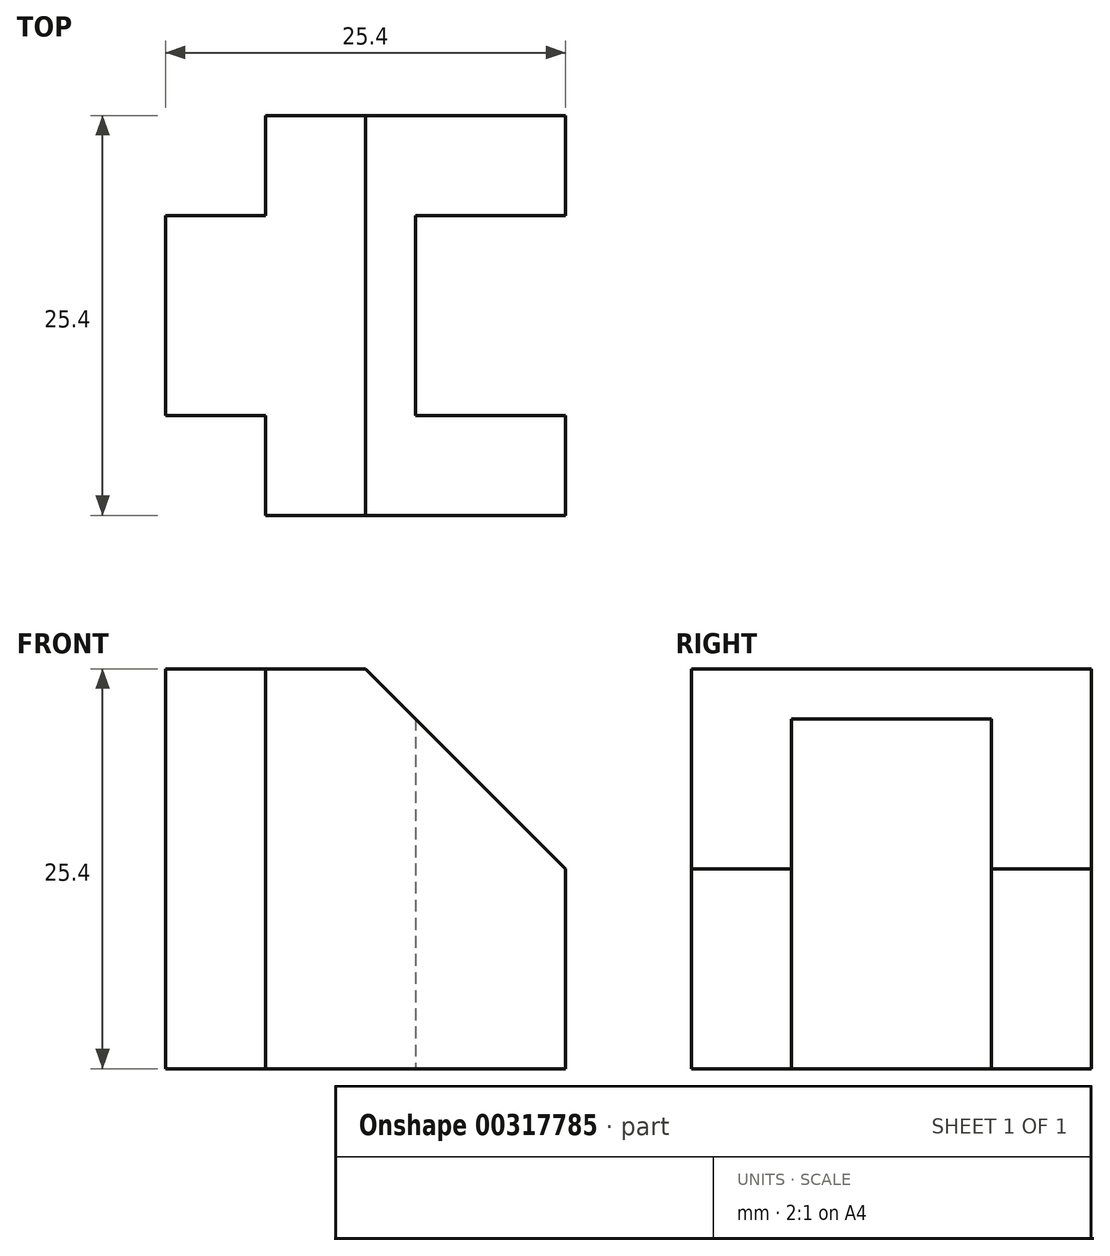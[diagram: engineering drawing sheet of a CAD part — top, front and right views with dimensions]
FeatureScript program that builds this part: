
annotation { "Feature Type Name" : "Feature", "Feature Type Description" : "" }
export const myFeature = defineFeature(function(context is Context, id is Id, definition is map)
    precondition{}
    {
        {
            var Q0;
            Q0=qCreatedBy(makeId("Front.planeOp"),FACE);
            var sketch = newSketch(context, id + "F0", { "sketchPlane" : qUnion([Q0])});
            skLineSegment(sketch, "E0", {"start": v(0, 0) * mm, "end": v(0, -25.4) * mm});
            skLineSegment(sketch, "E1", {"start": v(0, -25.4) * mm, "end": v(25.4, -25.4) * mm});
            skLineSegment(sketch, "E2", {"start": v(25.4, -25.4) * mm, "end": v(25.4, -12.7) * mm});
            skLineSegment(sketch, "E3", {"start": v(25.4, -12.7) * mm, "end": v(12.7, 0) * mm});
            skLineSegment(sketch, "E4", {"start": v(12.7, 0) * mm, "end": v(0, 0) * mm});
            skSolve(sketch);
        }
        {
            var Q0;
            Q0=makeQuery(id+"F0.imprint","IMPRINT",FACE,{"disambiguationData":[TD([[makeQuery(id+"F0.imprint","IMPRINT",EDGE,{"derivedFrom":sQuery(id+"F0.wireOp",EDGE,"E0")}),1.0]])]});
            extrude(context, id + "F1", {"entities" : qUnion([Q0]), "oppositeDirection" : true, "depth" : 25.4 * mm});
        }
        {
            var Q0;
            Q0=makeQuery(id+"F1.opExtrude","SWEPT_FACE",FACE,{"disambiguationData":[OSD([sQuery(id+"F0.wireOp",EDGE,"E4")])]});
            var sketch = newSketch(context, id + "F2", { "sketchPlane" : qUnion([Q0])});
            skLineSegment(sketch, "E5.bottom", {"start": v(0, 0) * mm, "end": v(6.35, 0) * mm});
            skLineSegment(sketch, "E5.top", {"start": v(0, 6.35) * mm, "end": v(6.35, 6.35) * mm});
            skLineSegment(sketch, "E5.left", {"start": v(0, 0) * mm, "end": v(0, 6.35) * mm});
            skLineSegment(sketch, "E5.right", {"start": v(6.35, 0) * mm, "end": v(6.35, 6.35) * mm});
            skLineSegment(sketch, "E6.bottom", {"start": v(0, 25.4) * mm, "end": v(6.35, 25.4) * mm});
            skLineSegment(sketch, "E6.top", {"start": v(0, 19.05) * mm, "end": v(6.35, 19.05) * mm});
            skLineSegment(sketch, "E6.left", {"start": v(0, 25.4) * mm, "end": v(0, 19.05) * mm});
            skLineSegment(sketch, "E6.right", {"start": v(6.35, 25.4) * mm, "end": v(6.35, 19.05) * mm});
            skSolve(sketch);
        }
        {
            var Q0;
            Q0=makeQuery(id+"F2.imprint","IMPRINT",FACE,{"disambiguationData":[TD([[makeQuery(id+"F2.imprint","IMPRINT",EDGE,{"derivedFrom":sQuery(id+"F2.wireOp",EDGE,"E6.bottom")}),1.0]])]});
            var Q1;
            Q1=makeQuery(id+"F2.imprint","IMPRINT",FACE,{"disambiguationData":[TD([[makeQuery(id+"F2.imprint","IMPRINT",EDGE,{"derivedFrom":sQuery(id+"F2.wireOp",EDGE,"E5.bottom")}),-1.0]])]});
            extrude(context, id + "F3", {"entities" : qUnion([Q0, Q1]), "operationType" : NewBodyOperationType.REMOVE, "endBound" : BoundingType.THROUGH_ALL, "oppositeDirection" : true, "depth" : 25.4 * mm});
        }
        {
            var Q0;
            Q0=makeQuery(id+"F1.opExtrude","SWEPT_FACE",FACE,{"disambiguationData":[OSD([sQuery(id+"F0.wireOp",EDGE,"E1")])]});
            var sketch = newSketch(context, id + "F4", { "sketchPlane" : qUnion([Q0])});
            skLineSegment(sketch, "E7.bottom", {"start": v(25.4, -19.05) * mm, "end": v(15.88, -19.05) * mm});
            skLineSegment(sketch, "E7.top", {"start": v(25.4, -6.35) * mm, "end": v(15.88, -6.35) * mm});
            skLineSegment(sketch, "E7.left", {"start": v(25.4, -19.05) * mm, "end": v(25.4, -6.35) * mm});
            skLineSegment(sketch, "E7.right", {"start": v(15.88, -19.05) * mm, "end": v(15.88, -6.35) * mm});
            skSolve(sketch);
        }
        {
            var Q0;
            Q0=makeQuery(id+"F4.imprint","IMPRINT",FACE,{"disambiguationData":[TD([[makeQuery(id+"F4.imprint","IMPRINT",EDGE,{"derivedFrom":sQuery(id+"F4.wireOp",EDGE,"E7.bottom")}),-1.0]])]});
            extrude(context, id + "F5", {"entities" : qUnion([Q0]), "operationType" : NewBodyOperationType.REMOVE, "endBound" : BoundingType.THROUGH_ALL, "oppositeDirection" : true, "depth" : 25.4 * mm});
        }
    });
